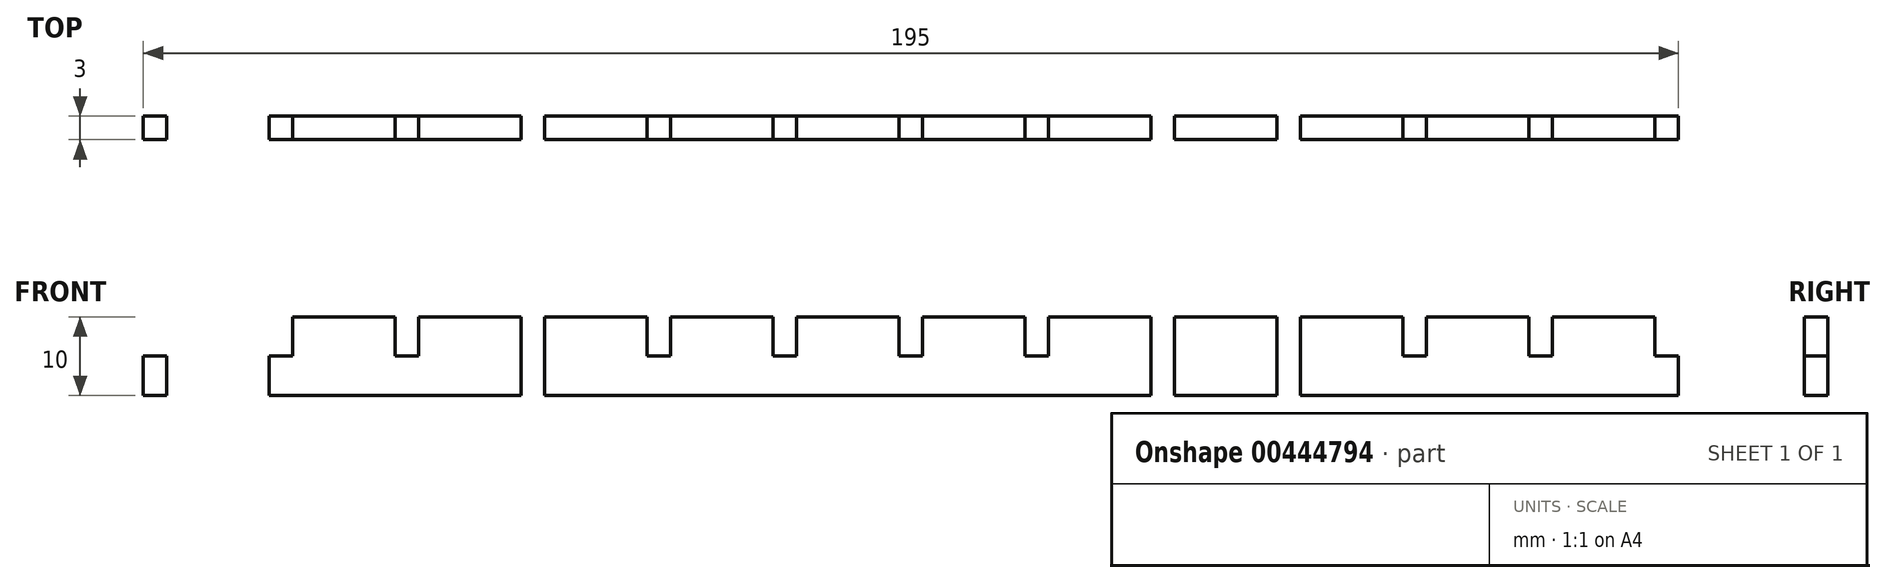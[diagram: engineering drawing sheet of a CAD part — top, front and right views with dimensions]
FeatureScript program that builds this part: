
annotation { "Feature Type Name" : "Feature", "Feature Type Description" : "" }
export const myFeature = defineFeature(function(context is Context, id is Id, definition is map)
    precondition{}
    {
        {
            var Q0;
            Q0=qCreatedBy(makeId("Front.planeOp"),FACE);
            var sketch = newSketch(context, id + "F0", { "sketchPlane" : qUnion([Q0])});
            skLineSegment(sketch, "E0", {"start": v(0, 0) * mm, "end": v(11.5, 0) * mm});
            skLineSegment(sketch, "E1", {"start": v(11.5, 0) * mm, "end": v(11.5, -2) * mm});
            skLineSegment(sketch, "E2", {"start": v(11.5, -2) * mm, "end": v(20.5, -2) * mm});
            skLineSegment(sketch, "E3", {"start": v(20.5, -2) * mm, "end": v(20.5, 0) * mm});
            skLineSegment(sketch, "E4", {"start": v(20.5, 0) * mm, "end": v(43.5, 0) * mm});
            skLineSegment(sketch, "E5", {"start": v(43.5, 0) * mm, "end": v(43.5, -2) * mm});
            skLineSegment(sketch, "E6", {"start": v(43.5, -2) * mm, "end": v(52.5, -2) * mm});
            skLineSegment(sketch, "E7", {"start": v(52.5, -2) * mm, "end": v(52.5, 0) * mm});
            skLineSegment(sketch, "E8", {"start": v(0, 0) * mm, "end": v(0, 10) * mm});
            skPoint(sketch, "E9.oppositeSnap0", {"position": v(0, 5) * mm});
            skLineSegment(sketch, "E9.bottom", {"start": v(0, 10) * mm, "end": v(-1.5, 10) * mm});
            skLineSegment(sketch, "E9.top", {"start": v(0, 5) * mm, "end": v(-1.5, 5) * mm});
            skLineSegment(sketch, "E9.left", {"start": v(0, 10) * mm, "end": v(0, 5) * mm});
            skLineSegment(sketch, "E9.right", {"start": v(-1.5, 10) * mm, "end": v(-1.5, 5) * mm});
            skLineSegment(sketch, "E10.bottom", {"start": v(14.5, 10) * mm, "end": v(17.5, 10) * mm});
            skLineSegment(sketch, "E10.top", {"start": v(14.5, 5) * mm, "end": v(17.5, 5) * mm});
            skLineSegment(sketch, "E10.left", {"start": v(14.5, 10) * mm, "end": v(14.5, 5) * mm});
            skLineSegment(sketch, "E10.right", {"start": v(17.5, 10) * mm, "end": v(17.5, 5) * mm});
            skLineSegment(sketch, "E11.top", {"start": v(0, 0) * mm, "end": v(-1.5, 0) * mm});
            skLineSegment(sketch, "E11.left", {"start": v(0, 5) * mm, "end": v(0, 0) * mm});
            skLineSegment(sketch, "E11.right", {"start": v(-1.5, 5) * mm, "end": v(-1.5, 0) * mm});
            skLineSegment(sketch, "E12.top", {"start": v(14.5, -2) * mm, "end": v(17.5, -2) * mm});
            skLineSegment(sketch, "E12.left", {"start": v(14.5, 5) * mm, "end": v(14.5, -2) * mm});
            skLineSegment(sketch, "E12.right", {"start": v(17.5, 5) * mm, "end": v(17.5, -2) * mm});
            skLineSegment(sketch, "E13.bottom", {"start": v(0, 10) * mm, "end": v(1.5, 10) * mm});
            skLineSegment(sketch, "E13.top", {"start": v(0, 5) * mm, "end": v(1.5, 5) * mm});
            skLineSegment(sketch, "E13.right", {"start": v(1.5, 10) * mm, "end": v(1.5, 5) * mm});
            skLineSegment(sketch, "E14.top", {"start": v(0, 0) * mm, "end": v(1.5, 0) * mm});
            skLineSegment(sketch, "E14.right", {"start": v(1.5, 5) * mm, "end": v(1.5, 0) * mm});
            skLineSegment(sketch, "E15.bottom", {"start": v(11.5, 10) * mm, "end": v(20.5, 10) * mm});
            skLineSegment(sketch, "E15.top", {"start": v(11.5, 13) * mm, "end": v(20.5, 13) * mm});
            skLineSegment(sketch, "E15.left", {"start": v(11.5, 10) * mm, "end": v(11.5, 13) * mm});
            skLineSegment(sketch, "E15.right", {"start": v(20.5, 10) * mm, "end": v(20.5, 13) * mm});
            skLineSegment(sketch, "E16", {"start": v(52.5, 0) * mm, "end": v(75.5, 0) * mm});
            skLineSegment(sketch, "E17", {"start": v(75.5, 0) * mm, "end": v(75.5, -2) * mm});
            skLineSegment(sketch, "E18", {"start": v(75.5, -2) * mm, "end": v(84.5, -2) * mm});
            skLineSegment(sketch, "E19", {"start": v(84.5, -2) * mm, "end": v(84.5, 0) * mm});
            skLineSegment(sketch, "E20", {"start": v(84.5, 0) * mm, "end": v(96, 0) * mm});
            skLineSegment(sketch, "E21", {"start": v(96, 0) * mm, "end": v(96, 19.13) * mm, "construction": true});
            skLineSegment(sketch, "E22", {"start": v(16, 10) * mm, "end": v(16, 11.65) * mm, "construction": true});
            skLineSegment(sketch, "E23.bottom", {"start": v(30.5, 0) * mm, "end": v(33.5, 0) * mm});
            skLineSegment(sketch, "E23.top", {"start": v(30.5, 5) * mm, "end": v(33.5, 5) * mm});
            skLineSegment(sketch, "E23.left", {"start": v(30.5, 0) * mm, "end": v(30.5, 5) * mm});
            skLineSegment(sketch, "E23.right", {"start": v(33.5, 0) * mm, "end": v(33.5, 5) * mm});
            skLineSegment(sketch, "E24.bottom", {"start": v(33.5, 5) * mm, "end": v(30.5, 5) * mm});
            skLineSegment(sketch, "E24.top", {"start": v(33.5, 10) * mm, "end": v(30.5, 10) * mm});
            skLineSegment(sketch, "E24.left", {"start": v(33.5, 5) * mm, "end": v(33.5, 10) * mm});
            skLineSegment(sketch, "E24.right", {"start": v(30.5, 5) * mm, "end": v(30.5, 10) * mm});
            skLineSegment(sketch, "E25", {"start": v(32, 0) * mm, "end": v(32, 2.31) * mm, "construction": true});
            skLineSegment(sketch, "E26.bottom", {"start": v(46.5, -2) * mm, "end": v(49.5, -2) * mm});
            skLineSegment(sketch, "E26.top", {"start": v(46.5, 5) * mm, "end": v(49.5, 5) * mm});
            skLineSegment(sketch, "E26.left", {"start": v(46.5, -2) * mm, "end": v(46.5, 5) * mm});
            skLineSegment(sketch, "E26.right", {"start": v(49.5, -2) * mm, "end": v(49.5, 5) * mm});
            skLineSegment(sketch, "E27.bottom", {"start": v(49.5, 5) * mm, "end": v(46.5, 5) * mm});
            skLineSegment(sketch, "E27.top", {"start": v(49.5, 10) * mm, "end": v(46.5, 10) * mm});
            skLineSegment(sketch, "E27.left", {"start": v(49.5, 5) * mm, "end": v(49.5, 10) * mm});
            skLineSegment(sketch, "E27.right", {"start": v(46.5, 5) * mm, "end": v(46.5, 10) * mm});
            skLineSegment(sketch, "E28.bottom", {"start": v(62.5, 0) * mm, "end": v(65.5, 0) * mm});
            skLineSegment(sketch, "E28.top", {"start": v(62.5, 5) * mm, "end": v(65.5, 5) * mm});
            skLineSegment(sketch, "E28.left", {"start": v(62.5, 0) * mm, "end": v(62.5, 5) * mm});
            skLineSegment(sketch, "E28.right", {"start": v(65.5, 0) * mm, "end": v(65.5, 5) * mm});
            skLineSegment(sketch, "E29.bottom", {"start": v(65.5, 5) * mm, "end": v(62.5, 5) * mm});
            skLineSegment(sketch, "E29.top", {"start": v(65.5, 10) * mm, "end": v(62.5, 10) * mm});
            skLineSegment(sketch, "E29.left", {"start": v(65.5, 5) * mm, "end": v(65.5, 10) * mm});
            skLineSegment(sketch, "E29.right", {"start": v(62.5, 5) * mm, "end": v(62.5, 10) * mm});
            skLineSegment(sketch, "E30.bottom", {"start": v(81.5, -2) * mm, "end": v(78.5, -2) * mm});
            skLineSegment(sketch, "E30.top", {"start": v(81.5, 5) * mm, "end": v(78.5, 5) * mm});
            skLineSegment(sketch, "E30.left", {"start": v(81.5, -2) * mm, "end": v(81.5, 5) * mm});
            skLineSegment(sketch, "E30.right", {"start": v(78.5, -2) * mm, "end": v(78.5, 5) * mm});
            skLineSegment(sketch, "E31.top", {"start": v(81.5, 10) * mm, "end": v(78.5, 10) * mm});
            skLineSegment(sketch, "E31.left", {"start": v(81.5, 5) * mm, "end": v(81.5, 10) * mm});
            skLineSegment(sketch, "E31.right", {"start": v(78.5, 5) * mm, "end": v(78.5, 10) * mm});
            skLineSegment(sketch, "E32.bottom", {"start": v(96, 0) * mm, "end": v(94.5, 0) * mm});
            skLineSegment(sketch, "E32.top", {"start": v(96, 5) * mm, "end": v(94.5, 5) * mm});
            skLineSegment(sketch, "E32.left", {"start": v(96, 0) * mm, "end": v(96, 5) * mm});
            skLineSegment(sketch, "E32.right", {"start": v(94.5, 0) * mm, "end": v(94.5, 5) * mm});
            skLineSegment(sketch, "E33.left", {"start": v(96, 5) * mm, "end": v(96, 5) * mm});
            skLineSegment(sketch, "E33.right", {"start": v(94.5, 5) * mm, "end": v(94.5, 5) * mm});
            skLineSegment(sketch, "E34.top", {"start": v(96, 10) * mm, "end": v(94.5, 10) * mm});
            skLineSegment(sketch, "E34.left", {"start": v(96, 5) * mm, "end": v(96, 10) * mm});
            skLineSegment(sketch, "E34.right", {"start": v(94.5, 5) * mm, "end": v(94.5, 10) * mm});
            skLineSegment(sketch, "E35", {"start": v(48, -2) * mm, "end": v(48, 0) * mm, "construction": true});
            skLineSegment(sketch, "E36", {"start": v(64, 0) * mm, "end": v(64, 2.67) * mm, "construction": true});
            skLineSegment(sketch, "E37", {"start": v(80, -2) * mm, "end": v(80, 0) * mm, "construction": true});
            skLineSegment(sketch, "E38", {"start": v(1.5, 10) * mm, "end": v(96, 10) * mm});
            skLineSegment(sketch, "E39.MirrorCS", {"start": v(96, 5) * mm, "end": v(97.5, 5) * mm});
            skLineSegment(sketch, "E40.MirrorCS", {"start": v(145.5, 5) * mm, "end": v(142.5, 5) * mm});
            skLineSegment(sketch, "E41.MirrorCS", {"start": v(110.5, 5) * mm, "end": v(113.5, 5) * mm});
            skLineSegment(sketch, "E42.MirrorCS", {"start": v(129.5, 5) * mm, "end": v(126.5, 5) * mm});
            skLineSegment(sketch, "E43.MirrorCS", {"start": v(177.5, 5) * mm, "end": v(174.5, 5) * mm});
            skLineSegment(sketch, "E44.MirrorCS", {"start": v(192, 5) * mm, "end": v(190.5, 5) * mm});
            skLineSegment(sketch, "E45.MirrorCS", {"start": v(192, 5) * mm, "end": v(193.5, 5) * mm});
            skLineSegment(sketch, "E46.MirrorCS", {"start": v(142.5, 5) * mm, "end": v(145.5, 5) * mm});
            skLineSegment(sketch, "E47.MirrorCS", {"start": v(126.5, 5) * mm, "end": v(129.5, 5) * mm});
            skLineSegment(sketch, "E48.MirrorCS", {"start": v(192, 10) * mm, "end": v(190.5, 10) * mm});
            skLineSegment(sketch, "E49.MirrorCS", {"start": v(171.5, -2) * mm, "end": v(171.5, 0) * mm});
            skLineSegment(sketch, "E50.MirrorCS", {"start": v(180.5, 0) * mm, "end": v(180.5, -2) * mm});
            skLineSegment(sketch, "E51.MirrorCS", {"start": v(177.5, 10) * mm, "end": v(174.5, 10) * mm});
            skLineSegment(sketch, "E52.MirrorCS", {"start": v(116.5, 0) * mm, "end": v(116.5, -2) * mm});
            skLineSegment(sketch, "E53.MirrorCS", {"start": v(177.5, -2) * mm, "end": v(174.5, -2) * mm});
            skLineSegment(sketch, "E54.MirrorCS", {"start": v(192, 0) * mm, "end": v(190.5, 0) * mm});
            skLineSegment(sketch, "E55.MirrorCS", {"start": v(126.5, 10) * mm, "end": v(129.5, 10) * mm});
            skLineSegment(sketch, "E56.MirrorCS", {"start": v(145.5, -2) * mm, "end": v(142.5, -2) * mm});
            skLineSegment(sketch, "E57.MirrorCS", {"start": v(110.5, -2) * mm, "end": v(113.5, -2) * mm});
            skLineSegment(sketch, "E58.MirrorCS", {"start": v(192, 0) * mm, "end": v(193.5, 0) * mm});
            skLineSegment(sketch, "E59.MirrorCS", {"start": v(96, 10) * mm, "end": v(97.5, 10) * mm});
            skLineSegment(sketch, "E60.MirrorCS", {"start": v(110.5, 10) * mm, "end": v(113.5, 10) * mm});
            skLineSegment(sketch, "E61.MirrorCS", {"start": v(142.5, 10) * mm, "end": v(145.5, 10) * mm});
            skLineSegment(sketch, "E62.MirrorCS", {"start": v(107.5, -2) * mm, "end": v(107.5, 0) * mm});
            skLineSegment(sketch, "E63.MirrorCS", {"start": v(192, 10) * mm, "end": v(193.5, 10) * mm});
            skLineSegment(sketch, "E64.MirrorCS", {"start": v(96, 0) * mm, "end": v(97.5, 0) * mm});
            skLineSegment(sketch, "E65.MirrorCS", {"start": v(139.5, -2) * mm, "end": v(139.5, 0) * mm});
            skLineSegment(sketch, "E66.MirrorCS", {"start": v(129.5, 0) * mm, "end": v(126.5, 0) * mm});
            skLineSegment(sketch, "E67.MirrorCS", {"start": v(148.5, 0) * mm, "end": v(148.5, -2) * mm});
            skLineSegment(sketch, "E68.MirrorCS", {"start": v(192, 5) * mm, "end": v(192, 0) * mm});
            skLineSegment(sketch, "E69.MirrorCS", {"start": v(112, -2) * mm, "end": v(112, 0) * mm, "construction": true});
            skLineSegment(sketch, "E70.MirrorCS", {"start": v(176, 10) * mm, "end": v(176, 11.65) * mm, "construction": true});
            skLineSegment(sketch, "E71.MirrorCS", {"start": v(192, 10) * mm, "end": v(192, 5) * mm});
            skLineSegment(sketch, "E72.MirrorCS", {"start": v(161.5, 0) * mm, "end": v(158.5, 0) * mm});
            skLineSegment(sketch, "E73.MirrorCS", {"start": v(128, 0) * mm, "end": v(128, 2.67) * mm, "construction": true});
            skLineSegment(sketch, "E74.MirrorCS", {"start": v(160, 0) * mm, "end": v(160, 2.31) * mm, "construction": true});
            skLineSegment(sketch, "E75.MirrorCS", {"start": v(144, -2) * mm, "end": v(144, 0) * mm, "construction": true});
            skLineSegment(sketch, "E76.MirrorCS", {"start": v(161.5, 5) * mm, "end": v(158.5, 5) * mm});
            skLineSegment(sketch, "E77.MirrorCS", {"start": v(171.5, 0) * mm, "end": v(148.5, 0) * mm});
            skLineSegment(sketch, "E78.MirrorCS", {"start": v(180.5, -2) * mm, "end": v(171.5, -2) * mm});
            skLineSegment(sketch, "E79.MirrorCS", {"start": v(192, 0) * mm, "end": v(180.5, 0) * mm});
            skLineSegment(sketch, "E80.MirrorCS", {"start": v(177.5, 10) * mm, "end": v(177.5, 5) * mm});
            skLineSegment(sketch, "E81.MirrorCS", {"start": v(158.5, 0) * mm, "end": v(158.5, 5) * mm});
            skLineSegment(sketch, "E82.MirrorCS", {"start": v(129.5, 0) * mm, "end": v(129.5, 5) * mm});
            skLineSegment(sketch, "E83.MirrorCS", {"start": v(97.5, 5) * mm, "end": v(97.5, 10) * mm});
            skPoint(sketch, "E84.MirrorP", {"position": v(192, 5) * mm});
            skLineSegment(sketch, "E85.MirrorCS", {"start": v(139.5, 0) * mm, "end": v(116.5, 0) * mm});
            skLineSegment(sketch, "E86.MirrorCS", {"start": v(126.5, 5) * mm, "end": v(126.5, 10) * mm});
            skLineSegment(sketch, "E87.MirrorCS", {"start": v(161.5, 5) * mm, "end": v(161.5, 10) * mm});
            skLineSegment(sketch, "E88.MirrorCS", {"start": v(180.5, 10) * mm, "end": v(180.5, 13) * mm});
            skLineSegment(sketch, "E89.MirrorCS", {"start": v(180.5, 13) * mm, "end": v(171.5, 13) * mm});
            skLineSegment(sketch, "E90.MirrorCS", {"start": v(158.5, 5) * mm, "end": v(158.5, 10) * mm});
            skLineSegment(sketch, "E91.MirrorCS", {"start": v(161.5, 0) * mm, "end": v(161.5, 5) * mm});
            skLineSegment(sketch, "E92.MirrorCS", {"start": v(107.5, 0) * mm, "end": v(96, 0) * mm});
            skLineSegment(sketch, "E93.MirrorCS", {"start": v(142.5, 5) * mm, "end": v(142.5, 10) * mm});
            skLineSegment(sketch, "E94.MirrorCS", {"start": v(193.5, 5) * mm, "end": v(193.5, 0) * mm});
            skLineSegment(sketch, "E95.MirrorCS", {"start": v(110.5, 5) * mm, "end": v(110.5, 10) * mm});
            skLineSegment(sketch, "E96.MirrorCS", {"start": v(180.5, 10) * mm, "end": v(171.5, 10) * mm});
            skLineSegment(sketch, "E97.MirrorCS", {"start": v(158.5, 10) * mm, "end": v(161.5, 10) * mm});
            skLineSegment(sketch, "E98.MirrorCS", {"start": v(145.5, 5) * mm, "end": v(145.5, 10) * mm});
            skLineSegment(sketch, "E99.MirrorCS", {"start": v(113.5, -2) * mm, "end": v(113.5, 5) * mm});
            skLineSegment(sketch, "E100.MirrorCS", {"start": v(174.5, 5) * mm, "end": v(174.5, -2) * mm});
            skLineSegment(sketch, "E101.MirrorCS", {"start": v(142.5, -2) * mm, "end": v(142.5, 5) * mm});
            skLineSegment(sketch, "E102.MirrorCS", {"start": v(113.5, 5) * mm, "end": v(113.5, 10) * mm});
            skLineSegment(sketch, "E103.MirrorCS", {"start": v(190.5, 10) * mm, "end": v(96, 10) * mm});
            skLineSegment(sketch, "E104.MirrorCS", {"start": v(190.5, 5) * mm, "end": v(190.5, 0) * mm});
            skLineSegment(sketch, "E105.MirrorCS", {"start": v(158.5, 5) * mm, "end": v(161.5, 5) * mm});
            skLineSegment(sketch, "E106.MirrorCS", {"start": v(126.5, 0) * mm, "end": v(126.5, 5) * mm});
            skLineSegment(sketch, "E107.MirrorCS", {"start": v(97.5, 0) * mm, "end": v(97.5, 5) * mm});
            skLineSegment(sketch, "E108.MirrorCS", {"start": v(174.5, 10) * mm, "end": v(174.5, 5) * mm});
            skLineSegment(sketch, "E109.MirrorCS", {"start": v(110.5, -2) * mm, "end": v(110.5, 5) * mm});
            skLineSegment(sketch, "E110.MirrorCS", {"start": v(177.5, 5) * mm, "end": v(177.5, -2) * mm});
            skLineSegment(sketch, "E111.MirrorCS", {"start": v(116.5, -2) * mm, "end": v(107.5, -2) * mm});
            skLineSegment(sketch, "E112.MirrorCS", {"start": v(145.5, -2) * mm, "end": v(145.5, 5) * mm});
            skLineSegment(sketch, "E113.MirrorCS", {"start": v(193.5, 10) * mm, "end": v(193.5, 5) * mm});
            skLineSegment(sketch, "E114.MirrorCS", {"start": v(129.5, 5) * mm, "end": v(129.5, 10) * mm});
            skLineSegment(sketch, "E115.MirrorCS", {"start": v(192, 0) * mm, "end": v(192, 10) * mm});
            skLineSegment(sketch, "E116.MirrorCS", {"start": v(148.5, -2) * mm, "end": v(139.5, -2) * mm});
            skLineSegment(sketch, "E117.MirrorCS", {"start": v(171.5, 10) * mm, "end": v(171.5, 13) * mm});
            skLineSegment(sketch, "E118.MirrorCS", {"start": v(190.5, 10) * mm, "end": v(190.5, 5) * mm});
            skLineSegment(sketch, "E119.top", {"start": v(14.5, 13) * mm, "end": v(17.5, 13) * mm});
            skLineSegment(sketch, "E119.left", {"start": v(14.5, 10) * mm, "end": v(14.5, 13) * mm});
            skLineSegment(sketch, "E119.right", {"start": v(17.5, 10) * mm, "end": v(17.5, 13) * mm});
            skLineSegment(sketch, "E120.bottom", {"start": v(174.5, 10) * mm, "end": v(177.5, 10) * mm});
            skLineSegment(sketch, "E120.top", {"start": v(174.5, 13) * mm, "end": v(177.5, 13) * mm});
            skLineSegment(sketch, "E120.left", {"start": v(174.5, 10) * mm, "end": v(174.5, 13) * mm});
            skLineSegment(sketch, "E120.right", {"start": v(177.5, 10) * mm, "end": v(177.5, 13) * mm});
            skLineSegment(sketch, "E121", {"start": v(11.5, 0) * mm, "end": v(180.5, 0) * mm});
            skSolve(sketch);
        }
        {
            var Q0;
            {var subQ5=sQuery(id+"F0.wireOp",EDGE,"E0");Q0=makeQuery(id+"F0.imprint","IMPRINT",FACE,{"disambiguationData":[TD([[makeQuery(id+"F0.imprint","IMPRINT",EDGE,{"derivedFrom":subQ5}),1.0]])]});}
            var Q1;
            {var subQ2=sQuery(id+"F0.wireOp",EDGE,"E10.right");Q1=makeQuery(id+"F0.imprint","IMPRINT",FACE,{"disambiguationData":[TD([[makeQuery(id+"F0.imprint","IMPRINT",EDGE,{"derivedFrom":subQ2}),1.0]])]});}
            var Q2;
            {var subQ1=sQuery(id+"F0.wireOp",EDGE,"E23.right");Q2=makeQuery(id+"F0.imprint","IMPRINT",FACE,{"disambiguationData":[TD([[makeQuery(id+"F0.imprint","IMPRINT",EDGE,{"derivedFrom":subQ1}),-1.0]])]});}
            var Q3;
            {var subQ2=sQuery(id+"F0.wireOp",EDGE,"E27.left");Q3=makeQuery(id+"F0.imprint","IMPRINT",FACE,{"disambiguationData":[TD([[makeQuery(id+"F0.imprint","IMPRINT",EDGE,{"derivedFrom":subQ2}),-1.0]])]});}
            var Q4;
            {var subQ1=sQuery(id+"F0.wireOp",EDGE,"E28.right");Q4=makeQuery(id+"F0.imprint","IMPRINT",FACE,{"disambiguationData":[TD([[makeQuery(id+"F0.imprint","IMPRINT",EDGE,{"derivedFrom":subQ1}),-1.0]])]});}
            var Q5;
            {var subQ2=sQuery(id+"F0.wireOp",EDGE,"E31.left");Q5=makeQuery(id+"F0.imprint","IMPRINT",FACE,{"disambiguationData":[TD([[makeQuery(id+"F0.imprint","IMPRINT",EDGE,{"derivedFrom":subQ2}),-1.0]])]});}
            var Q6;
            {var subQ2=sQuery(id+"F0.wireOp",EDGE,"E83.MirrorCS");Q6=makeQuery(id+"F0.imprint","IMPRINT",FACE,{"disambiguationData":[TD([[makeQuery(id+"F0.imprint","IMPRINT",EDGE,{"derivedFrom":subQ2}),-1.0]])]});}
            var Q7;
            {var subQ1=sQuery(id+"F0.wireOp",EDGE,"E86.MirrorCS");Q7=makeQuery(id+"F0.imprint","IMPRINT",FACE,{"disambiguationData":[TD([[makeQuery(id+"F0.imprint","IMPRINT",EDGE,{"derivedFrom":subQ1}),1.0]])]});}
            var Q8;
            {var subQ6=sQuery(id+"F0.wireOp",EDGE,"E82.MirrorCS");Q8=makeQuery(id+"F0.imprint","IMPRINT",FACE,{"disambiguationData":[TD([[makeQuery(id+"F0.imprint","IMPRINT",EDGE,{"derivedFrom":subQ6}),-1.0]])]});}
            var Q9;
            {var subQ7=sQuery(id+"F0.wireOp",EDGE,"E81.MirrorCS");Q9=makeQuery(id+"F0.imprint","IMPRINT",FACE,{"disambiguationData":[TD([[makeQuery(id+"F0.imprint","IMPRINT",EDGE,{"derivedFrom":subQ7}),1.0]])]});}
            var Q10;
            {var subQ7=sQuery(id+"F0.wireOp",EDGE,"E87.MirrorCS");Q10=makeQuery(id+"F0.imprint","IMPRINT",FACE,{"disambiguationData":[TD([[makeQuery(id+"F0.imprint","IMPRINT",EDGE,{"derivedFrom":subQ7}),-1.0]])]});}
            var Q11;
            {var subQ1=sQuery(id+"F0.wireOp",EDGE,"E80.MirrorCS");Q11=makeQuery(id+"F0.imprint","IMPRINT",FACE,{"disambiguationData":[TD([[makeQuery(id+"F0.imprint","IMPRINT",EDGE,{"derivedFrom":subQ1}),1.0]])]});}
            var Q12;
            Q12=makeQuery(id+"F0.imprint","IMPRINT",FACE,{"disambiguationData":[TD([[makeQuery(id+"F0.imprint","IMPRINT",EDGE,{"derivedFrom":sQuery(id+"F0.wireOp",EDGE,"E13.top")}),-1.0]])]});
            var Q13;
            Q13=makeQuery(id+"F0.imprint","IMPRINT",FACE,{"disambiguationData":[TD([[makeQuery(id+"F0.imprint","IMPRINT",EDGE,{"derivedFrom":sQuery(id+"F0.wireOp",EDGE,"E9.top")}),1.0]])]});
            var Q14;
            {var subQ0=sQuery(id+"F0.wireOp",EDGE,"E10.top");Q14=makeQuery(id+"F0.imprint","IMPRINT",FACE,{"disambiguationData":[TD([[makeQuery(id+"F0.imprint","IMPRINT",EDGE,{"derivedFrom":subQ0}),-1.0]])]});}
            var Q15;
            {var subQ0=sQuery(id+"F0.wireOp",EDGE,"E23.left");Q15=makeQuery(id+"F0.imprint","IMPRINT",FACE,{"disambiguationData":[TD([[makeQuery(id+"F0.imprint","IMPRINT",EDGE,{"derivedFrom":subQ0}),-1.0]])]});}
            var Q16;
            {var subQ0=sQuery(id+"F0.wireOp",EDGE,"E27.bottom");Q16=makeQuery(id+"F0.imprint","IMPRINT",FACE,{"disambiguationData":[TD([[makeQuery(id+"F0.imprint","IMPRINT",EDGE,{"derivedFrom":subQ0}),1.0]])]});}
            var Q17;
            {var subQ0=sQuery(id+"F0.wireOp",EDGE,"E28.left");Q17=makeQuery(id+"F0.imprint","IMPRINT",FACE,{"disambiguationData":[TD([[makeQuery(id+"F0.imprint","IMPRINT",EDGE,{"derivedFrom":subQ0}),-1.0]])]});}
            var Q18;
            {var subQ0=sQuery(id+"F0.wireOp",EDGE,"E30.top");Q18=makeQuery(id+"F0.imprint","IMPRINT",FACE,{"disambiguationData":[TD([[makeQuery(id+"F0.imprint","IMPRINT",EDGE,{"derivedFrom":subQ0}),1.0]])]});}
            var Q19;
            Q19=makeQuery(id+"F0.imprint","IMPRINT",FACE,{"disambiguationData":[TD([[makeQuery(id+"F0.imprint","IMPRINT",EDGE,{"derivedFrom":sQuery(id+"F0.wireOp",EDGE,"E39.MirrorCS")}),-1.0]])]});
            var Q20;
            {var subQ0=sQuery(id+"F0.wireOp",EDGE,"E41.MirrorCS");Q20=makeQuery(id+"F0.imprint","IMPRINT",FACE,{"disambiguationData":[TD([[makeQuery(id+"F0.imprint","IMPRINT",EDGE,{"derivedFrom":subQ0}),-1.0]])]});}
            var Q21;
            Q21=makeQuery(id+"F0.imprint","IMPRINT",FACE,{"disambiguationData":[TD([[makeQuery(id+"F0.imprint","IMPRINT",EDGE,{"derivedFrom":sQuery(id+"F0.wireOp",EDGE,"E47.MirrorCS")}),-1.0]])]});
            var Q22;
            {var subQ0=sQuery(id+"F0.wireOp",EDGE,"E46.MirrorCS");Q22=makeQuery(id+"F0.imprint","IMPRINT",FACE,{"disambiguationData":[TD([[makeQuery(id+"F0.imprint","IMPRINT",EDGE,{"derivedFrom":subQ0}),-1.0]])]});}
            var Q23;
            {var subQ0=sQuery(id+"F0.wireOp",EDGE,"E81.MirrorCS");Q23=makeQuery(id+"F0.imprint","IMPRINT",FACE,{"disambiguationData":[TD([[makeQuery(id+"F0.imprint","IMPRINT",EDGE,{"derivedFrom":subQ0}),-1.0]])]});}
            var Q24;
            {var subQ0=sQuery(id+"F0.wireOp",EDGE,"E32.right");Q24=makeQuery(id+"F0.imprint","IMPRINT",FACE,{"disambiguationData":[TD([[makeQuery(id+"F0.imprint","IMPRINT",EDGE,{"derivedFrom":subQ0}),-1.0]])]});}
            var Q25;
            {var subQ0=sQuery(id+"F0.wireOp",EDGE,"E43.MirrorCS");Q25=makeQuery(id+"F0.imprint","IMPRINT",FACE,{"disambiguationData":[TD([[makeQuery(id+"F0.imprint","IMPRINT",EDGE,{"derivedFrom":subQ0}),1.0]])]});}
            var Q26;
            {var subQ0=sQuery(id+"F0.wireOp",EDGE,"E44.MirrorCS");Q26=makeQuery(id+"F0.imprint","IMPRINT",FACE,{"disambiguationData":[TD([[makeQuery(id+"F0.imprint","IMPRINT",EDGE,{"derivedFrom":subQ0}),1.0]])]});}
            var Q27;
            {var subQ0=sQuery(id+"F0.wireOp",EDGE,"E45.MirrorCS");Q27=makeQuery(id+"F0.imprint","IMPRINT",FACE,{"disambiguationData":[TD([[makeQuery(id+"F0.imprint","IMPRINT",EDGE,{"derivedFrom":subQ0}),-1.0]])]});}
            extrude(context, id + "F1", {"entities" : qUnion([Q0, Q1, Q2, Q3, Q4, Q5, Q6, Q7, Q8, Q9, Q10, Q11, Q12, Q13, Q14, Q15, Q16, Q17, Q18, Q19, Q20, Q21, Q22, Q23, Q24, Q25, Q26, Q27]), "depth" : 3 * mm});
        }
    });
